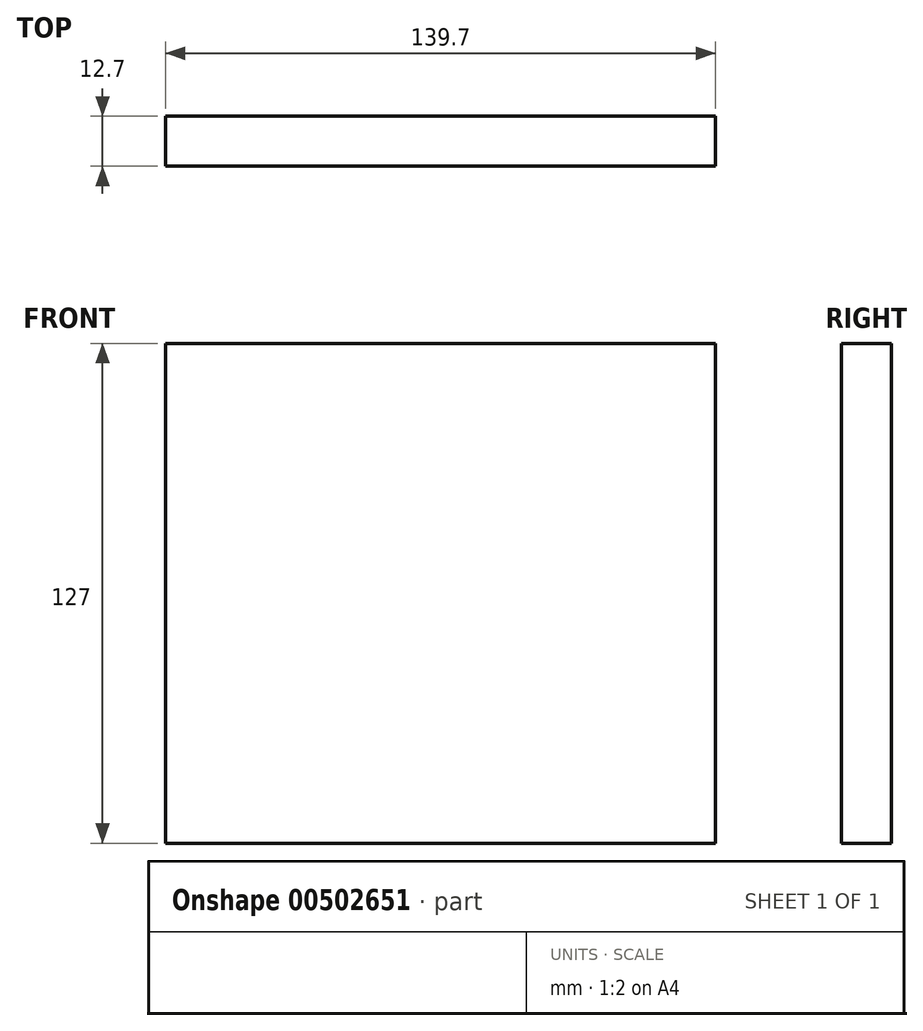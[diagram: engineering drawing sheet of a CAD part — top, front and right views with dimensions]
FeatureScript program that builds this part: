
annotation { "Feature Type Name" : "Feature", "Feature Type Description" : "" }
export const myFeature = defineFeature(function(context is Context, id is Id, definition is map)
    precondition{}
    {
        {
            var Q0;
            Q0=qCreatedBy(makeId("Front.planeOp"),FACE);
            var sketch = newSketch(context, id + "F0", { "sketchPlane" : qUnion([Q0])});
            skLineSegment(sketch, "E0.bottom", {"start": v(0, 0) * mm, "end": v(139.7, 0) * mm});
            skLineSegment(sketch, "E0.top", {"start": v(0, 127) * mm, "end": v(139.7, 127) * mm});
            skLineSegment(sketch, "E0.left", {"start": v(0, 0) * mm, "end": v(0, 127) * mm});
            skLineSegment(sketch, "E0.right", {"start": v(139.7, 0) * mm, "end": v(139.7, 127) * mm});
            skSolve(sketch);
        }
        {
            var Q0;
            Q0=makeQuery(id+"F0.imprint","IMPRINT",FACE,{"disambiguationData":[TD([[makeQuery(id+"F0.imprint","IMPRINT",EDGE,{"derivedFrom":sQuery(id+"F0.wireOp",EDGE,"E0.bottom")}),1.0]])]});
            extrude(context, id + "F1", {"entities" : qUnion([Q0]), "depth" : 12.7 * mm});
        }
    });
